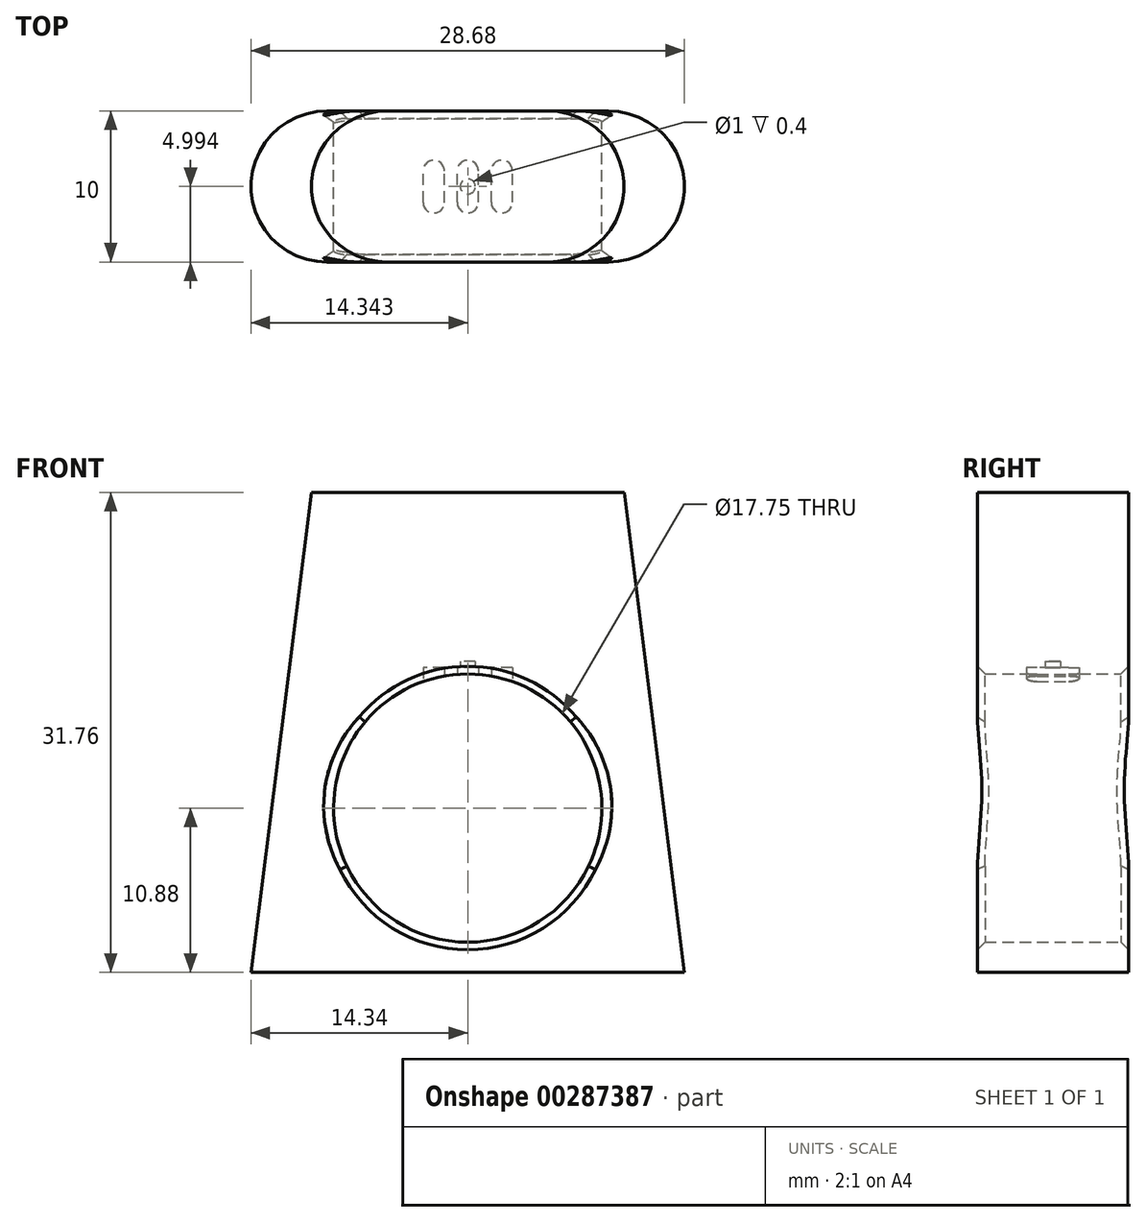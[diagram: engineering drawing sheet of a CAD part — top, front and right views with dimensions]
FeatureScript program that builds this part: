
annotation { "Feature Type Name" : "Feature", "Feature Type Description" : "" }
export const myFeature = defineFeature(function(context is Context, id is Id, definition is map)
    precondition{}
    {
        {
            var Q0;
            Q0=qCreatedBy(makeId("Front.planeOp"),FACE);
            var sketch = newSketch(context, id + "F0", { "sketchPlane" : qUnion([Q0])});
            skCircle(sketch, "E0", {"center": v(0, 0) * mm, "radius": 8.88 * mm});
            skLineSegment(sketch, "E1", {"start": v(-10.35, 20.88) * mm, "end": v(-14.34, -10.88) * mm});
            skLineSegment(sketch, "E2", {"start": v(-14.34, -10.88) * mm, "end": v(0, -10.88) * mm});
            skLineSegment(sketch, "E3", {"start": v(-10.35, 20.88) * mm, "end": v(0, 20.88) * mm});
            skLineSegment(sketch, "E4.MirrorCS", {"start": v(10.35, 20.88) * mm, "end": v(0, 20.88) * mm});
            skLineSegment(sketch, "E5.MirrorCS", {"start": v(10.35, 20.88) * mm, "end": v(14.34, -10.88) * mm});
            skLineSegment(sketch, "E6.MirrorCS", {"start": v(14.34, -10.88) * mm, "end": v(0, -10.88) * mm});
            skSolve(sketch);
        }
        {
            var Q0;
            Q0=makeQuery(id+"F0.imprint","IMPRINT",FACE,{"disambiguationData":[TD([[makeQuery(id+"F0.imprint","IMPRINT",EDGE,{"derivedFrom":sQuery(id+"F0.wireOp",EDGE,"E0")}),-1.0]])]});
            extrude(context, id + "F1", {"entities" : qUnion([Q0]), "depth" : 5 * mm, "hasSecondDirection" : true, "secondDirectionOppositeDirection" : true, "secondDirectionDepth" : 5 * mm});
        }
        {
            var Q0;
            Q0=makeQuery(id+"F1.opExtrude","CAP_EDGE",EDGE,{"disambiguationData":[OSD([sQuery(id+"F0.wireOp",EDGE,"E5.MirrorCS")])],"isStart":false});
            var Q1;
            Q1=makeQuery(id+"F1.opExtrude","CAP_EDGE",EDGE,{"disambiguationData":[OSD([sQuery(id+"F0.wireOp",EDGE,"E5.MirrorCS")])],"isStart":true});
            var Q2;
            Q2=makeQuery(id+"F1.opExtrude","CAP_EDGE",EDGE,{"disambiguationData":[OSD([sQuery(id+"F0.wireOp",EDGE,"E1")])],"isStart":false});
            var Q3;
            Q3=makeQuery(id+"F1.opExtrude","CAP_EDGE",EDGE,{"disambiguationData":[OSD([sQuery(id+"F0.wireOp",EDGE,"E1")])],"isStart":true});
            fillet(context, id + "F2", {"entities" : qUnion([Q0, Q1, Q2, Q3]), "radius" : 5 * mm, "tangentPropagation" : true, "allowEdgeOverflow" : false});
        }
        {
            var Q0;
            Q0=makeQuery(id+"F1.opExtrude","CAP_EDGE",EDGE,{"disambiguationData":[OSD([sQuery(id+"F0.wireOp",EDGE,"E0")])],"isStart":false});
            var Q1;
            Q1=makeQuery(id+"F1.opExtrude","CAP_EDGE",EDGE,{"disambiguationData":[OSD([sQuery(id+"F0.wireOp",EDGE,"E0")])],"isStart":true});
            chamfer(context, id + "F3", {"entities" : qUnion([Q0, Q1]), "width" : .5 * mm, "tangentPropagation" : true});
        }
        {
            var Q0;
            Q0=qCreatedBy(makeId("Top.planeOp"),FACE);
            var sketch = newSketch(context, id + "F4", { "sketchPlane" : qUnion([Q0])});
            skLineSegment(sketch, "E7.bottom", {"start": v(-4.82, -0.07) * mm, "end": v(-4.82, -0.07) * mm});
            skLineSegment(sketch, "E7.top", {"start": v(-4.82, -3.56) * mm, "end": v(-4.82, -3.56) * mm});
            skLineSegment(sketch, "E7.left", {"start": v(-2.95, 1.04) * mm, "end": v(-2.95, -1.06) * mm});
            skLineSegment(sketch, "E7.right", {"start": v(-1.55, 1.04) * mm, "end": v(-1.55, -1.06) * mm});
            skLineSegment(sketch, "E8.bottom", {"start": v(-2.57, -0.06) * mm, "end": v(-2.57, -0.06) * mm});
            skLineSegment(sketch, "E8.top", {"start": v(-2.57, -3.56) * mm, "end": v(-2.57, -3.56) * mm});
            skLineSegment(sketch, "E8.left", {"start": v(-0.7, 1.04) * mm, "end": v(-0.7, -1.05) * mm});
            skLineSegment(sketch, "E8.right", {"start": v(0.7, 1.04) * mm, "end": v(0.7, -1.05) * mm});
            skLineSegment(sketch, "E9.bottom", {"start": v(-0.32, -0.06) * mm, "end": v(-0.32, -0.06) * mm});
            skLineSegment(sketch, "E9.top", {"start": v(-0.32, -3.56) * mm, "end": v(-0.32, -3.56) * mm});
            skLineSegment(sketch, "E9.left", {"start": v(1.56, 1.04) * mm, "end": v(1.56, -1.05) * mm});
            skLineSegment(sketch, "E9.right", {"start": v(2.96, 1.04) * mm, "end": v(2.96, -1.05) * mm});
            skPoint(sketch, "E10.visualSharp", {"position": v(-2.95, 1.74) * mm});
            skArc(sketch, "E10.filletArc", {"start": v(-2.25, 1.74) * mm, "mid": v(-2.74, 1.53) * mm, "end": v(-2.95, 1.04) * mm});
            skPoint(sketch, "E11.visualSharp", {"position": v(-1.55, 1.74) * mm});
            skArc(sketch, "E11.filletArc", {"start": v(-1.55, 1.04) * mm, "mid": v(-1.76, 1.53) * mm, "end": v(-2.25, 1.74) * mm});
            skPoint(sketch, "E12.visualSharp", {"position": v(-2.95, -1.76) * mm});
            skArc(sketch, "E12.filletArc", {"start": v(-2.95, -1.06) * mm, "mid": v(-2.74, -1.55) * mm, "end": v(-2.25, -1.76) * mm});
            skPoint(sketch, "E13.visualSharp", {"position": v(-1.55, -1.76) * mm});
            skArc(sketch, "E13.filletArc", {"start": v(-2.25, -1.76) * mm, "mid": v(-1.76, -1.55) * mm, "end": v(-1.55, -1.06) * mm});
            skPoint(sketch, "E14.visualSharp", {"position": v(-0.7, 1.74) * mm});
            skArc(sketch, "E14.filletArc", {"start": v(0, 1.74) * mm, "mid": v(-0.5, 1.54) * mm, "end": v(-0.7, 1.04) * mm});
            skPoint(sketch, "E15.visualSharp", {"position": v(0.7, 1.74) * mm});
            skArc(sketch, "E15.filletArc", {"start": v(0.7, 1.04) * mm, "mid": v(0.5, 1.54) * mm, "end": v(0, 1.74) * mm});
            skPoint(sketch, "E16.visualSharp", {"position": v(-0.7, -1.75) * mm});
            skArc(sketch, "E16.filletArc", {"start": v(-0.7, -1.05) * mm, "mid": v(-0.5, -1.55) * mm, "end": v(0, -1.75) * mm});
            skPoint(sketch, "E17.visualSharp", {"position": v(0.7, -1.75) * mm});
            skArc(sketch, "E17.filletArc", {"start": v(0, -1.75) * mm, "mid": v(0.5, -1.55) * mm, "end": v(0.7, -1.05) * mm});
            skPoint(sketch, "E18.visualSharp", {"position": v(1.56, 1.74) * mm});
            skArc(sketch, "E18.filletArc", {"start": v(2.26, 1.74) * mm, "mid": v(1.76, 1.54) * mm, "end": v(1.56, 1.04) * mm});
            skPoint(sketch, "E19.visualSharp", {"position": v(2.96, 1.74) * mm});
            skArc(sketch, "E19.filletArc", {"start": v(2.96, 1.04) * mm, "mid": v(2.75, 1.54) * mm, "end": v(2.26, 1.74) * mm});
            skPoint(sketch, "E20.visualSharp", {"position": v(2.96, -1.75) * mm});
            skArc(sketch, "E20.filletArc", {"start": v(2.26, -1.75) * mm, "mid": v(2.75, -1.55) * mm, "end": v(2.96, -1.05) * mm});
            skPoint(sketch, "E21.visualSharp", {"position": v(1.56, -1.75) * mm});
            skArc(sketch, "E21.filletArc", {"start": v(1.56, -1.05) * mm, "mid": v(1.76, -1.55) * mm, "end": v(2.26, -1.75) * mm});
            skLineSegment(sketch, "E22", {"start": v(0, 1.74) * mm, "end": v(0, -1.75) * mm, "construction": true});
            skPoint(sketch, "E23", {"position": v(0, 0) * mm});
            skCircle(sketch, "E24", {"center": v(0, 0) * mm, "radius": 0.5 * mm});
            skSolve(sketch);
        }
        {
            var Q0;
            Q0=makeQuery(id+"F4.imprint","IMPRINT",FACE,{"disambiguationData":[TD([[makeQuery(id+"F4.imprint","IMPRINT",EDGE,{"derivedFrom":sQuery(id+"F4.wireOp",EDGE,"E9.left")}),1.0]])]});
            var Q1;
            Q1=makeQuery(id+"F4.imprint","IMPRINT",FACE,{"disambiguationData":[TD([[makeQuery(id+"F4.imprint","IMPRINT",EDGE,{"derivedFrom":sQuery(id+"F4.wireOp",EDGE,"E8.left")}),1.0]])]});
            var Q2;
            Q2=makeQuery(id+"F4.imprint","IMPRINT",FACE,{"disambiguationData":[TD([[makeQuery(id+"F4.imprint","IMPRINT",EDGE,{"derivedFrom":sQuery(id+"F4.wireOp",EDGE,"E7.left")}),1.0]])]});
            extrude(context, id + "F5", {"entities" : qUnion([Q0, Q1, Q2]), "operationType" : NewBodyOperationType.REMOVE, "offsetDistance" : 25 * mm, "depth" : 9.3 * mm});
        }
        {
            var Q0;
            Q0=makeQuery(id+"F4.imprint","IMPRINT",FACE,{"disambiguationData":[TD([[makeQuery(id+"F4.imprint","IMPRINT",EDGE,{"derivedFrom":sQuery(id+"F4.wireOp",EDGE,"E24")}),1.0]])]});
            extrude(context, id + "F6", {"entities" : qUnion([Q0]), "operationType" : NewBodyOperationType.REMOVE, "depth" : 9.7 * mm});
        }
    });
